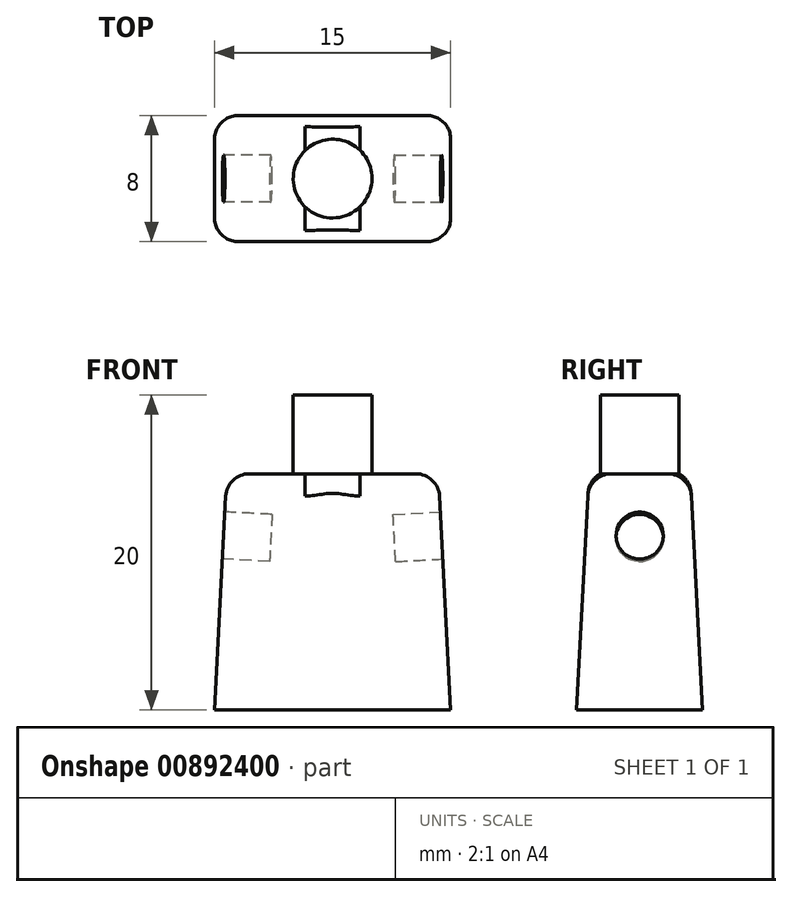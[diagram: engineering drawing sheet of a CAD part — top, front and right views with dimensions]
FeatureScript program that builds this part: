
annotation { "Feature Type Name" : "Feature", "Feature Type Description" : "" }
export const myFeature = defineFeature(function(context is Context, id is Id, definition is map)
    precondition{}
    {
        {
            var Q0;
            Q0=qCreatedBy(makeId("Top.planeOp"),FACE);
            var sketch = newSketch(context, id + "F0", { "sketchPlane" : qUnion([Q0])});
            skLineSegment(sketch, "E0.bottom", {"start": v(7.5, -4) * mm, "end": v(-7.5, -4) * mm});
            skLineSegment(sketch, "E0.top", {"start": v(7.5, 4) * mm, "end": v(-7.5, 4) * mm});
            skLineSegment(sketch, "E0.left", {"start": v(7.5, -4) * mm, "end": v(7.5, 4) * mm});
            skLineSegment(sketch, "E0.right", {"start": v(-7.5, -4) * mm, "end": v(-7.5, 4) * mm});
            skPoint(sketch, "E0.middle", {"position": v(0, 0) * mm});
            skSolve(sketch);
        }
        {
            var Q0;
            Q0 = qSketchRegion(id + "F0", true);
            extrude(context, id + "F1", {"entities" : qUnion([Q0]), "depth" : 15 * mm, "offsetDistance" : 25.4 * mm, "hasDraft" : true, "draftAngle" : 3 * degree, "draftPullDirection" : true});
        }
        {
            var Q0;
            Q0=makeQuery(id+"F1.opExtrude","CAP_FACE",FACE,{"disambiguationData":[OSD([sQuery(id+"F0.wireOp",EDGE,"E0.bottom"),sQuery(id+"F0.wireOp",EDGE,"E0.top"),sQuery(id+"F0.wireOp",EDGE,"E0.left"),sQuery(id+"F0.wireOp",EDGE,"E0.right")])],"isStart":false});
            var sketch = newSketch(context, id + "F2", { "sketchPlane" : qUnion([Q0])});
            skCircle(sketch, "E1", {"center": v(0, 0) * mm, "radius": 2.5 * mm});
            skSolve(sketch);
        }
        {
            var Q0;
            Q0=makeQuery(id+"F2.imprint","IMPRINT",FACE,{"disambiguationData":[TD([[makeQuery(id+"F2.imprint","IMPRINT",EDGE,{"derivedFrom":sQuery(id+"F2.wireOp",EDGE,"E1")}),1.0]])]});
            extrude(context, id + "F3", {"entities" : qUnion([Q0]), "operationType" : NewBodyOperationType.ADD, "depth" : 5 * mm, "offsetDistance" : 25.4 * mm});
        }
        {
            var Q0;
            Q0=makeQuery(id+"F1.opExtrude","CAP_EDGE",EDGE,{"disambiguationData":[OSD([sQuery(id+"F0.wireOp",EDGE,"E0.top")])],"isStart":false});
            var Q1;
            Q1=makeQuery(id+"F1.opExtrude","CAP_EDGE",EDGE,{"disambiguationData":[OSD([sQuery(id+"F0.wireOp",EDGE,"E0.right")])],"isStart":false});
            var Q2;
            Q2=makeQuery(id+"F1.opExtrude","CAP_EDGE",EDGE,{"disambiguationData":[OSD([sQuery(id+"F0.wireOp",EDGE,"E0.bottom")])],"isStart":false});
            var Q3;
            Q3=makeQuery(id+"F1.opExtrude","CAP_EDGE",EDGE,{"disambiguationData":[OSD([sQuery(id+"F0.wireOp",EDGE,"E0.left")])],"isStart":false});
            var Q4;
            Q4=makeQuery(id+"F1.opExtrude","SWEPT_EDGE",EDGE,{"disambiguationData":[OSD([sQuery(id+"F0.wireOp",EDGE,"E0.top"),sQuery(id+"F0.wireOp",EDGE,"E0.left")])]});
            var Q5;
            Q5=makeQuery(id+"F1.opExtrude","SWEPT_EDGE",EDGE,{"disambiguationData":[OSD([sQuery(id+"F0.wireOp",EDGE,"E0.top"),sQuery(id+"F0.wireOp",EDGE,"E0.right")])]});
            var Q6;
            Q6=makeQuery(id+"F1.opExtrude","SWEPT_EDGE",EDGE,{"disambiguationData":[OSD([sQuery(id+"F0.wireOp",EDGE,"E0.bottom"),sQuery(id+"F0.wireOp",EDGE,"E0.right")])]});
            var Q7;
            Q7=makeQuery(id+"F1.opExtrude","SWEPT_EDGE",EDGE,{"disambiguationData":[OSD([sQuery(id+"F0.wireOp",EDGE,"E0.bottom"),sQuery(id+"F0.wireOp",EDGE,"E0.left")])]});
            fillet(context, id + "F4", {"entities" : qUnion([Q0, Q1, Q2, Q3, Q4, Q5, Q6, Q7]), "radius" : 1.5 * mm, "tangentPropagation" : true, "allowEdgeOverflow" : false});
        }
        {
            var Q0;
            Q0=makeQuery(id+"F1.opExtrude","SWEPT_FACE",FACE,{"disambiguationData":[OSD([sQuery(id+"F0.wireOp",EDGE,"E0.right")])]});
            var sketch = newSketch(context, id + "F5", { "sketchPlane" : qUnion([Q0])});
            skCircle(sketch, "E2", {"center": v(0, 10.7) * mm, "radius": 1.5 * mm});
            skSolve(sketch);
        }
        {
            var Q0;
            Q0=makeQuery(id+"F5.imprint","IMPRINT",FACE,{"disambiguationData":[TD([[makeQuery(id+"F5.imprint","IMPRINT",EDGE,{"derivedFrom":sQuery(id+"F5.wireOp",EDGE,"E2")}),1.0]])]});
            extrude(context, id + "F6", {"entities" : qUnion([Q0]), "operationType" : NewBodyOperationType.REMOVE, "oppositeDirection" : true, "depth" : 3 * mm, "offsetDistance" : 25.4 * mm});
        }
        {
            var Q0;
            Q0=makeQuery(id+"F1.opExtrude","SWEPT_FACE",FACE,{"disambiguationData":[OSD([sQuery(id+"F0.wireOp",EDGE,"E0.left")])]});
            var sketch = newSketch(context, id + "F7", { "sketchPlane" : qUnion([Q0])});
            skCircle(sketch, "E3", {"center": v(0, 10.7) * mm, "radius": 1.5 * mm});
            skSolve(sketch);
        }
        {
            var Q0;
            Q0=makeQuery(id+"F7.imprint","IMPRINT",FACE,{"disambiguationData":[TD([[makeQuery(id+"F7.imprint","IMPRINT",EDGE,{"derivedFrom":sQuery(id+"F7.wireOp",EDGE,"E3")}),1.0]])]});
            extrude(context, id + "F8", {"entities" : qUnion([Q0]), "operationType" : NewBodyOperationType.REMOVE, "oppositeDirection" : true, "depth" : 3 * mm, "offsetDistance" : 25.4 * mm});
        }
    });
